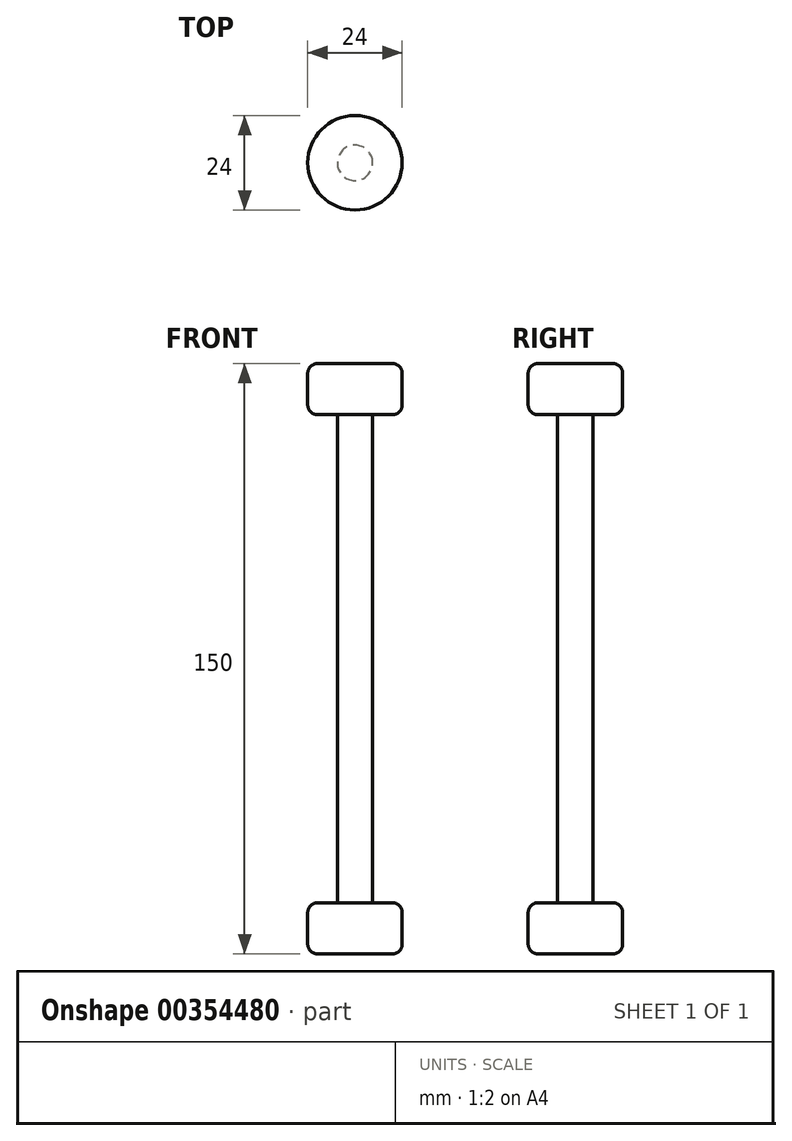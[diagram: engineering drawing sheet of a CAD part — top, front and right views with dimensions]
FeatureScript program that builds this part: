
annotation { "Feature Type Name" : "Feature", "Feature Type Description" : "" }
export const myFeature = defineFeature(function(context is Context, id is Id, definition is map)
    precondition{}
    {
        {
            var Q0;
            Q0=qCreatedBy(makeId("Top.planeOp"),FACE);
            var sketch = newSketch(context, id + "F0", { "sketchPlane" : qUnion([Q0])});
            skCircle(sketch, "E0", {"center": v(0, 0) * mm, "radius": 4.5 * mm});
            skCircle(sketch, "E1", {"center": v(0, 0) * mm, "radius": 12 * mm});
            skSolve(sketch);
        }
        {
            var Q0;
            Q0=makeQuery(id+"F0.imprint","IMPRINT",FACE,{"disambiguationData":[TD([[makeQuery(id+"F0.imprint","IMPRINT",EDGE,{"derivedFrom":sQuery(id+"F0.wireOp",EDGE,"E0")}),1.0]])]});
            var Q1;
            Q1=sQuery(id+"F0.wireOp",EDGE,"E0");
            extrude(context, id + "F1", {"entities" : qUnion([Q0]), "surfaceEntities" : qUnion([Q1]), "depth" : 150 * mm});
        }
        {
            var Q0;
            Q0=makeQuery(id+"F0.imprint","IMPRINT",FACE,{"disambiguationData":[TD([[makeQuery(id+"F0.imprint","IMPRINT",EDGE,{"derivedFrom":sQuery(id+"F0.wireOp",EDGE,"E0")}),-1.0]])]});
            var Q1;
            Q1=sQuery(id+"F0.wireOp",EDGE,"E1");
            extrude(context, id + "F2", {"entities" : qUnion([Q0]), "operationType" : NewBodyOperationType.ADD, "surfaceEntities" : qUnion([Q1]), "depth" : 13 * mm});
        }
        {
            var Q0;
            Q0=makeQuery(id+"F1.opExtrude","CAP_FACE",FACE,{"disambiguationData":[OSD([sQuery(id+"F0.wireOp",EDGE,"E0")])],"isStart":false});
            var sketch = newSketch(context, id + "F3", { "sketchPlane" : qUnion([Q0])});
            skCircle(sketch, "E2", {"center": v(0, 0) * mm, "radius": 12 * mm});
            skSolve(sketch);
        }
        {
            var Q0;
            Q0=makeQuery(id+"F3.imprint","IMPRINT",FACE,{"disambiguationData":[TD([[makeQuery(id+"F3.imprint","IMPRINT",EDGE,{"derivedFrom":sQuery(id+"F3.wireOp",EDGE,"E2")}),1.0]])]});
            extrude(context, id + "F4", {"entities" : qUnion([Q0]), "operationType" : NewBodyOperationType.ADD, "oppositeDirection" : true, "depth" : 13 * mm});
        }
        {
            var Q0;
            Q0=makeQuery(id+"F4.opExtrude","CAP_EDGE",EDGE,{"disambiguationData":[OSD([sQuery(id+"F3.wireOp",EDGE,"E2")])],"isStart":true});
            var Q1;
            Q1=makeQuery(id+"F4.opExtrude","CAP_EDGE",EDGE,{"disambiguationData":[OSD([sQuery(id+"F3.wireOp",EDGE,"E2")])],"isStart":false});
            var Q2;
            Q2=makeQuery(id+"F2.opExtrude","CAP_EDGE",EDGE,{"disambiguationData":[OSD([sQuery(id+"F0.wireOp",EDGE,"E1")])],"isStart":false});
            var Q3;
            Q3=makeQuery(id+"F2.opExtrude","CAP_EDGE",EDGE,{"disambiguationData":[OSD([sQuery(id+"F0.wireOp",EDGE,"E1")])],"isStart":true});
            fillet(context, id + "F5", {"entities" : qUnion([Q0, Q1, Q2, Q3]), "radius" : 2.5 * mm, "tangentPropagation" : true, "allowEdgeOverflow" : false});
        }
    });
